MODEL slx_5f61af2557be
CONFIG AbsTol = auto
CONFIG EnableMultiTasking = off
CONFIG FixedStep = auto
CONFIG MaxStep = auto
CONFIG MinStep = auto
CONFIG RelTol = 1e-3
CONFIG SampleTimeConstraint = Unconstrained
CONFIG SolverName = ode23s
CONFIG StartTime = 0.0
CONFIG StopTime = 173.890
BLOCK [Constant] Constant
  Value = 0
BLOCK [Constant] Constant1
  Value = 0.013
BLOCK [FromWorkspace] From Workspace
  SampleTime = -1
  VariableName = pdl_percent
BLOCK [FromWorkspace] From Workspace1
  SampleTime = -1
  VariableName = left_mtr_tmp
BLOCK [FromWorkspace] From Workspace2
  VariableName = right_mtr_tmp
BLOCK [Gain] Gain
  Gain = 1/M
BLOCK [Gain] Gain2
  Gain = M/4*g
  NameLocation = right
BLOCK [Gain] Gain3
  Gain = 8.5/(M/4)
BLOCK [SubSystem] MATLAB Function2
  ErrorFcn = Stateflow.Translate.translate
  PermitHierarchicalResolution = ExplicitOnly
  SFBlockType = MATLAB Function
  TreatAsAtomicUnit = on
BLOCK [Demux] MATLAB Function2/ Demux 
  Outputs = 1
BLOCK [S-Function] MATLAB Function2/ SFunction 
  EnableBusSupport = on
  FunctionName = sf_sfun
  PortCounts = [2 2]
  SFcnIsStateOwnerBlock = off
  SFunctionDeploymentMode = off
  Tag = Stateflow S-Function 13
BLOCK [Terminator] MATLAB Function2/ Terminator 
BLOCK [Outport] MATLAB Function2/frr
BLOCK [Inport] MATLAB Function2/prev_wheel_ang_vel
BLOCK [Inport] MATLAB Function2/rolling_coeff
  Port = 2
BLOCK [Memory] Memory
BLOCK [SubSystem] Old_Slip_Controller
  PortSchema = {"entries":[{"content":{"sides":[{"content":{"connectorIds":["Out1"]},"type":"ConnectorPlacement.EquallySpacedRectSide","uuid":"3d629ccf-3120-465c-b95a-c1e856ea96ae"},{"content":{"side":"RIGHT"},"type":"ConnectorPlacement.EquallySpacedRectSide","uuid":"39ac0bf8-cdbe-4e91-b33c-4b222cbdbfda"},{"content":{"connectorIds":["In1","In2","In3"],"side":"TOP"},"type":"ConnectorPlacement.EquallySpacedRectSid...<+360ch>
BLOCK [Outport] Old_Slip_Controller/Error Torque
BLOCK [From] Old_Slip_Controller/From1
  GotoTag = slip_err
BLOCK [From] Old_Slip_Controller/From4
  GotoTag = curr_slip
BLOCK [Gain] Old_Slip_Controller/Gain
  Gain = 1/10
BLOCK [Gain] Old_Slip_Controller/Gain2
  Gain = 1/R
BLOCK [Goto] Old_Slip_Controller/Goto
  GotoTag = pid_slip_err
BLOCK [Goto] Old_Slip_Controller/Goto1
  GotoTag = slip_err
BLOCK [Goto] Old_Slip_Controller/Goto3
  GotoTag = curr_slip
BLOCK [Reference] Old_Slip_Controller/PID Controller (2DOF)  REF=slpidlib/PID Controller (2DOF)
  LibrarySourceBlock = simulink/Continuous/PID Controller (2DOF)
  SourceBlock = slpidlib/PID Controller (2DOF)
  SourceType = PID 2dof
BLOCK [Sum] Old_Slip_Controller/Subtract1
  IconShape = rectangular
  Inputs = +-
BLOCK [SubSystem] Old_Slip_Controller/Vehicle_vel_x_err
  ErrorFcn = Stateflow.Translate.translate
  PermitHierarchicalResolution = ExplicitOnly
  SFBlockType = MATLAB Function
  TreatAsAtomicUnit = on
BLOCK [Demux] Old_Slip_Controller/Vehicle_vel_x_err/ Demux 
  Outputs = 1
BLOCK [S-Function] Old_Slip_Controller/Vehicle_vel_x_err/ SFunction 
  EnableBusSupport = on
  FunctionName = sf_sfun
  PortCounts = [3 2]
  SFcnIsStateOwnerBlock = off
  SFunctionDeploymentMode = off
  Tag = Stateflow S-Function 4
BLOCK [Terminator] Old_Slip_Controller/Vehicle_vel_x_err/ Terminator 
BLOCK [Inport] Old_Slip_Controller/Vehicle_vel_x_err/accel_x
  Port = 3
BLOCK [Outport] Old_Slip_Controller/Vehicle_vel_x_err/err_veh_speed_x
BLOCK [Inport] Old_Slip_Controller/Vehicle_vel_x_err/pid_slip_err
BLOCK [Inport] Old_Slip_Controller/Vehicle_vel_x_err/wheel_speed_x
  Port = 2
BLOCK [Inport] Old_Slip_Controller/curr_slip_ratio
  Port = 3
BLOCK [Constant] Old_Slip_Controller/ideal_slip
  Value = 0.05
BLOCK [Scope] Old_Slip_Controller/slip_err
  Floating = off
  NumInputPorts = 4
  ScopeSpecificationString = Simulink.scopes.TimeScopeBlockCfg('CurrentConfiguration', extmgr.ConfigurationSet(extmgr.Configuration('Core','General UI',true),extmgr.Configuration('Core','Source UI',true),extmgr.Configuration('Sources','WiredSimulink',true,'DataLoggingVariableName','ScopeData1'),extmgr.Configuration('Visuals','Time Domain',true,'SerializedDisplays',{struct('MinYLimReal','-0.14568','MaxYLimReal','0.05647','YLab...<+1578ch>
BLOCK [Scope] Old_Slip_Controller/speed//accel-comparison
  Floating = off
  NumInputPorts = 4
  ScopeSpecificationString = Simulink.scopes.TimeScopeBlockCfg('CurrentConfiguration', extmgr.ConfigurationSet(extmgr.Configuration('Core','General UI',true),extmgr.Configuration('Core','Source UI',true),extmgr.Configuration('Sources','WiredSimulink',true,'DataLoggingVariableName','ScopeData2'),extmgr.Configuration('Visuals','Time Domain',true,'SerializedDisplays',{struct('MinYLimReal','62.2804','MaxYLimReal','173.12651','YLa...<+1560ch>
BLOCK [Constant] Old_Slip_Controller/target_err
  Value = 0
BLOCK [Inport] Old_Slip_Controller/vehicle_accel_x
BLOCK [Inport] Old_Slip_Controller/wheel_v_x
  Port = 2
BLOCK [Saturate] Saturation
  LowerLimit = 0
  UpperLimit = 1
BLOCK [Scope] Scope
  Floating = off
  NumInputPorts = 3
  ScopeSpecificationString = Simulink.scopes.TimeScopeBlockCfg('CurrentConfiguration', extmgr.ConfigurationSet(extmgr.Configuration('Core','General UI',true),extmgr.Configuration('Core','Source UI',true),extmgr.Configuration('Sources','WiredSimulink',true,'DataLoggingVariableName','ScopeData1'),extmgr.Configuration('Visuals','Time Domain',true,'SerializedDisplays',{struct('MinYLimReal','-1.9125','MaxYLimReal','17.2125','YLabe...<+1499ch>
BLOCK [Scope] Scope1
  Floating = off
  NumInputPorts = 1
  ScopeSpecificationString = Simulink.scopes.TimeScopeBlockCfg('CurrentConfiguration', extmgr.ConfigurationSet(extmgr.Configuration('Core','General UI',true),extmgr.Configuration('Core','Source UI',true),extmgr.Configuration('Sources','WiredSimulink',true,'DataLoggingVariableName','ScopeData1'),extmgr.Configuration('Visuals','Time Domain',true,'SerializedDisplays',{struct('MinYLimReal','-0.04536','MaxYLimReal','0.40826','YLab...<+1463ch>
BLOCK [SubSystem] Slip Controller 
  PortSchema = {"entries":[{"content":{"sides":[{"content":{"connectorIds":["Out1"]},"type":"ConnectorPlacement.EquallySpacedRectSide","uuid":"9ab017ca-b6c6-4a97-8642-adcc6752da5c"},{"content":{"connectorIds":["In1"],"side":"RIGHT"},"type":"ConnectorPlacement.EquallySpacedRectSide","uuid":"f028d533-9454-44bd-bcae-05da9a7b9b8f"},{"content":{"side":"TOP"},"type":"ConnectorPlacement.EquallySpacedRectSide","uuid":"7...<+348ch>
BLOCK [From] Slip Controller /From
  GotoTag = ideal_slip_ratio
BLOCK [Goto] Slip Controller /Goto
  GotoTag = ideal_slip_ratio
BLOCK [Reference] Slip Controller /PID Controller (2DOF)  REF=slpidlib/PID Controller (2DOF)
  LibrarySourceBlock = simulink/Continuous/PID Controller (2DOF)
  SourceBlock = slpidlib/PID Controller (2DOF)
  SourceType = PID 2dof
BLOCK [Sum] Slip Controller /Sum
  Inputs = |+-
BLOCK [Outport] Slip Controller /T_correction
BLOCK [Inport] Slip Controller /curr_slip
BLOCK [Constant] Slip Controller /ideal slip
  Value = 0.05
BLOCK [Scope] Slip Controller /slip
  Floating = off
  NumInputPorts = 3
  ScopeSpecificationString = Simulink.scopes.TimeScopeBlockCfg('CurrentConfiguration', extmgr.ConfigurationSet(extmgr.Configuration('Core','General UI',true),extmgr.Configuration('Core','Source UI',true),extmgr.Configuration('Sources','WiredSimulink',true,'DataLoggingVariableName','ScopeData1'),extmgr.Configuration('Visuals','Time Domain',true,'SerializedDisplays',{struct('MinYLimReal','-0.08166','MaxYLimReal','0.08642','YLab...<+1556ch>
BLOCK [Sum] Sum
  Inputs = |+-
BLOCK [Sum] Sum1
  Inputs = |-+
BLOCK [Sum] T_err
  Inputs = |+-
BLOCK [SubSystem] Torque Controller
BLOCK [Constant] Torque Controller/Car_Power_Limit_kW
  Value = 40
BLOCK [Constant] Torque Controller/Constant
BLOCK [Constant] Torque Controller/Constant1
  Value = 80.0/30.0
BLOCK [SubSystem] Torque Controller/MATLAB Function
  ErrorFcn = Stateflow.Translate.translate
  PermitHierarchicalResolution = ExplicitOnly
  SFBlockType = MATLAB Function
  TreatAsAtomicUnit = on
BLOCK [Demux] Torque Controller/MATLAB Function/ Demux 
  Outputs = 1
BLOCK [S-Function] Torque Controller/MATLAB Function/ SFunction 
  EnableBusSupport = on
  FunctionName = sf_sfun
  PortCounts = [3 2]
  SFcnIsStateOwnerBlock = off
  SFunctionDeploymentMode = off
  Tag = Stateflow S-Function 9
BLOCK [Terminator] Torque Controller/MATLAB Function/ Terminator 
BLOCK [Inport] Torque Controller/MATLAB Function/conversion_factor
  Port = 2
BLOCK [Inport] Torque Controller/MATLAB Function/inverter_power
BLOCK [Outport] Torque Controller/MATLAB Function/motor_RPM
BLOCK [Inport] Torque Controller/MATLAB Function/torque_request
  Port = 3
BLOCK [MinMax] Torque Controller/Max
  Function = max
  Inputs = 2
BLOCK [MinMax] Torque Controller/Max_Allowable_Power
  Inputs = 2
BLOCK [MinMax] Torque Controller/Max_Full_Throttle_Power
  Inputs = 2
BLOCK [SubSystem] Torque Controller/Max_Motor_Temp_Power
  ErrorFcn = Stateflow.Translate.translate
  PermitHierarchicalResolution = ExplicitOnly
  SFBlockType = MATLAB Function
  TreatAsAtomicUnit = on
BLOCK [Demux] Torque Controller/Max_Motor_Temp_Power/ Demux 
  Outputs = 1
BLOCK [S-Function] Torque Controller/Max_Motor_Temp_Power/ SFunction 
  EnableBusSupport = on
  FunctionName = sf_sfun
  PortCounts = [4 2]
  SFcnIsStateOwnerBlock = off
  SFunctionDeploymentMode = off
  Tag = Stateflow S-Function 3
BLOCK [Terminator] Torque Controller/Max_Motor_Temp_Power/ Terminator 
BLOCK [Outport] Torque Controller/Max_Motor_Temp_Power/avail_power
BLOCK [Inport] Torque Controller/Max_Motor_Temp_Power/curr_power_limit
  Port = 4
BLOCK [Inport] Torque Controller/Max_Motor_Temp_Power/decrementing_ratio
BLOCK [Inport] Torque Controller/Max_Motor_Temp_Power/max_motor_temp
  Port = 2
BLOCK [Inport] Torque Controller/Max_Motor_Temp_Power/motor_cutoff_temp
  Port = 3
BLOCK [Product] Torque Controller/Pedal_Based_Power_Request
BLOCK [SubSystem] Torque Controller/Pedal_Based_Torque_Mapping
  ErrorFcn = Stateflow.Translate.translate
  PermitHierarchicalResolution = ExplicitOnly
  SFBlockType = MATLAB Function
  TreatAsAtomicUnit = on
BLOCK [Demux] Torque Controller/Pedal_Based_Torque_Mapping/ Demux 
  Outputs = 1
BLOCK [S-Function] Torque Controller/Pedal_Based_Torque_Mapping/ SFunction 
  EnableBusSupport = on
  FunctionName = sf_sfun
  PortCounts = [1 2]
  SFcnIsStateOwnerBlock = off
  SFunctionDeploymentMode = off
  Tag = Stateflow S-Function 8
BLOCK [Terminator] Torque Controller/Pedal_Based_Torque_Mapping/ Terminator 
BLOCK [Outport] Torque Controller/Pedal_Based_Torque_Mapping/T
BLOCK [Inport] Torque Controller/Pedal_Based_Torque_Mapping/p_a
BLOCK [SubSystem] Torque Controller/Power_To_Torque
  ErrorFcn = Stateflow.Translate.translate
  PermitHierarchicalResolution = ExplicitOnly
  SFBlockType = MATLAB Function
  TreatAsAtomicUnit = on
BLOCK [Demux] Torque Controller/Power_To_Torque/ Demux 
  Outputs = 1
BLOCK [S-Function] Torque Controller/Power_To_Torque/ SFunction 
  EnableBusSupport = on
  FunctionName = sf_sfun
  PortCounts = [6 2]
  SFcnIsStateOwnerBlock = off
  SFunctionDeploymentMode = off
  Tag = Stateflow S-Function 7
BLOCK [Terminator] Torque Controller/Power_To_Torque/ Terminator 
BLOCK [Outport] Torque Controller/Power_To_Torque/Power_to_Torque
BLOCK [Inport] Torque Controller/Power_To_Torque/cl
  Port = 4
BLOCK [Inport] Torque Controller/Power_To_Torque/cr
  Port = 5
BLOCK [Inport] Torque Controller/Power_To_Torque/left_motor_speed
BLOCK [Inport] Torque Controller/Power_To_Torque/p_to_t_conversion_factor
  Port = 6
BLOCK [Inport] Torque Controller/Power_To_Torque/power_KW_input
  Port = 3
BLOCK [Inport] Torque Controller/Power_To_Torque/right_motor_speed
  Port = 2
BLOCK [Scope] Torque Controller/Scope
  Floating = off
  NumInputPorts = 3
  ScopeSpecificationString = Simulink.scopes.TimeScopeBlockCfg('CurrentConfiguration', extmgr.ConfigurationSet(extmgr.Configuration('Core','General UI',true),extmgr.Configuration('Core','Source UI',true),extmgr.Configuration('Sources','WiredSimulink',true,'DataLoggingVariableName','ScopeData1'),extmgr.Configuration('Visuals','Time Domain',true,'SerializedDisplays',{struct('MinYLimReal','-11.25','MaxYLimReal','101.25','YLabelR...<+1624ch>
BLOCK [SubSystem] Torque Controller/Steering_Angle_To_Delta
  ErrorFcn = Stateflow.Translate.translate
  PermitHierarchicalResolution = ExplicitOnly
  SFBlockType = MATLAB Function
  TreatAsAtomicUnit = on
BLOCK [Demux] Torque Controller/Steering_Angle_To_Delta/ Demux 
  Outputs = 1
BLOCK [S-Function] Torque Controller/Steering_Angle_To_Delta/ SFunction 
  EnableBusSupport = on
  FunctionName = sf_sfun
  PortCounts = [3 2]
  SFcnIsStateOwnerBlock = off
  SFunctionDeploymentMode = off
  Tag = Stateflow S-Function 6
BLOCK [Terminator] Torque Controller/Steering_Angle_To_Delta/ Terminator 
BLOCK [Inport] Torque Controller/Steering_Angle_To_Delta/TRACK_WIDTH_mm
  Port = 2
BLOCK [Inport] Torque Controller/Steering_Angle_To_Delta/WHEELBASE_mm
  Port = 3
BLOCK [Outport] Torque Controller/Steering_Angle_To_Delta/delta
BLOCK [Inport] Torque Controller/Steering_Angle_To_Delta/wheel_angle_deg
BLOCK [Sum] Torque Controller/Sum
  Inputs = |++
BLOCK [Sum] Torque Controller/Sum1
  Inputs = |+-
BLOCK [SubSystem] Torque Controller/Torque_To_Send
  ErrorFcn = Stateflow.Translate.translate
  PermitHierarchicalResolution = ExplicitOnly
  SFBlockType = MATLAB Function
  TreatAsAtomicUnit = on
BLOCK [Demux] Torque Controller/Torque_To_Send/ Demux 
  Outputs = 1
BLOCK [S-Function] Torque Controller/Torque_To_Send/ SFunction 
  EnableBusSupport = on
  FunctionName = sf_sfun
  PortCounts = [4 2]
  SFcnIsStateOwnerBlock = off
  SFunctionDeploymentMode = off
  Tag = Stateflow S-Function 5
BLOCK [Terminator] Torque Controller/Torque_To_Send/ Terminator 
BLOCK [Inport] Torque Controller/Torque_To_Send/cl
BLOCK [Outport] Torque Controller/Torque_To_Send/computed_torque
BLOCK [Inport] Torque Controller/Torque_To_Send/cr
  Port = 2
BLOCK [Inport] Torque Controller/Torque_To_Send/request_torque
  Port = 3
BLOCK [Inport] Torque Controller/Torque_To_Send/torque_lim
  Port = 4
BLOCK [Constant] Torque Controller/Track_width_mm
  Value = 1100
BLOCK [Constant] Torque Controller/Track_width_mm1
  Value = 1550
BLOCK [Outport] Torque Controller/computedTorque
BLOCK [Inport] Torque Controller/input
BLOCK [Inport] Torque Controller/left_motor_temp
  Port = 3
BLOCK [Inport] Torque Controller/motor_cutoff_temp
  Port = 2
BLOCK [Constant] Torque Controller/p2t_conversion_factor
  Value = 9550
BLOCK [Inport] Torque Controller/right_motor_temp
  Port = 4
BLOCK [Inport] Torque Controller/wheel_angle_deg
  Port = 5
BLOCK [Inport] Torque Controller/wheel_v_x
  Port = 6
BLOCK [MinMax] clamp1
  Function = max
  Inputs = 2
BLOCK [MinMax] clamp2
  Inputs = 2
BLOCK [Constant] cutoff_temp
  Value = 90
BLOCK [Gain] drag_f_form
  Gain = 0.5* mass_den * Cd * Af
BLOCK [Constant] max_torque
  Value = 90
BLOCK [Constant] min_torque
  Value = 0
BLOCK [Math] square
  Operator = square
BLOCK [SubSystem] tire_model
BLOCK [Constant] tire_model/Constant
  Value = 0
BLOCK [Outport] tire_model/F_x
  Port = 2
BLOCK [From] tire_model/From
  GotoTag = vehicle_v_x
  NameLocation = top
BLOCK [From] tire_model/From F_x
  GotoTag = F_x
BLOCK [FromWorkspace] tire_model/From Workspace
  SampleTime = -1
  VariableName = recorded_vel
BLOCK [From] tire_model/From1
  GotoTag = vehicle_a_x
  NameLocation = top
BLOCK [From] tire_model/From2
  GotoTag = slip_ratio
BLOCK [From] tire_model/From3
  GotoTag = wheel_ang_v_x
BLOCK [From] tire_model/From4
  GotoTag = vehicle_v_x
BLOCK [Gain] tire_model/Gain
  Gain = 1/J_w
BLOCK [Gain] tire_model/Gain1
  Gain = R
BLOCK [Gain] tire_model/Gain2
  Gain = M/4*g
  NameLocation = top
BLOCK [Gain] tire_model/Gain4
  Gain = R
  NameLocation = right
BLOCK [Goto] tire_model/Goto
  GotoTag = vehicle_a_x
BLOCK [Goto] tire_model/Goto1
  GotoTag = vehicle_v_x
BLOCK [Goto] tire_model/Goto2
  GotoTag = slip_ratio
BLOCK [Goto] tire_model/Goto3
  GotoTag = wheel_ang_v_x
BLOCK [Integrator] tire_model/Integrator
BLOCK [Integrator] tire_model/Integrator1
BLOCK [MinMax] tire_model/Max
  Function = max
  Inputs = 2
BLOCK [SubSystem] tire_model/Pacejka Magic Formula
  ErrorFcn = Stateflow.Translate.translate
  NameLocation = top
  PermitHierarchicalResolution = ExplicitOnly
  SFBlockType = MATLAB Function
  TreatAsAtomicUnit = on
BLOCK [Demux] tire_model/Pacejka Magic Formula/ Demux 
  Outputs = 1
BLOCK [S-Function] tire_model/Pacejka Magic Formula/ SFunction 
  EnableBusSupport = on
  FunctionName = sf_sfun
  Parameters = B,C,D,E
  PortCounts = [1 2]
  SFcnIsStateOwnerBlock = off
  SFunctionDeploymentMode = off
  Tag = Stateflow S-Function 1
BLOCK [Terminator] tire_model/Pacejka Magic Formula/ Terminator 
BLOCK [Outport] tire_model/Pacejka Magic Formula/friction_coeff
BLOCK [Inport] tire_model/Pacejka Magic Formula/lambda
BLOCK [Scope] tire_model/Scope
  Floating = off
  NumInputPorts = 2
  ScopeSpecificationString = Simulink.scopes.TimeScopeBlockCfg('CurrentConfiguration', extmgr.ConfigurationSet(extmgr.Configuration('Core','General UI',true),extmgr.Configuration('Core','Source UI',true),extmgr.Configuration('Sources','WiredSimulink',true,'DataLoggingVariableName','ScopeData1'),extmgr.Configuration('Visuals','Time Domain',true,'SerializedDisplays',{struct('MinYLimReal','-5.07777','MaxYLimReal','45.69989','YLa...<+1469ch>
BLOCK [Scope] tire_model/Slip & friction
  Floating = on
  NumInputPorts = 1
  ScopeSpecificationString = Simulink.scopes.TimeScopeBlockCfg('CurrentConfiguration', extmgr.ConfigurationSet(extmgr.Configuration('Core','General UI',true),extmgr.Configuration('Core','Source UI',true),extmgr.Configuration('Sources','WiredSimulink',true,'DataLoggingVariableName','ScopeData1'),extmgr.Configuration('Visuals','Time Domain',true,'SerializedDisplays',{struct('MinYLimReal','-0.08597','MaxYLimReal','0.7737','YLabe...<+1562ch>
BLOCK [Sum] tire_model/Sum
  Inputs = |+-
BLOCK [Inport] tire_model/T_in
  Port = 2
BLOCK [Scope] tire_model/Torques and speeds
  Floating = on
  NumInputPorts = 1
  ScopeSpecificationString = Simulink.scopes.TimeScopeBlockCfg('CurrentConfiguration', extmgr.ConfigurationSet(extmgr.Configuration('Core','General UI',true,'FigureColor',[0.156862745098039 0.156862745098039 0.156862745098039]),extmgr.Configuration('Core','Source UI',true),extmgr.Configuration('Sources','WiredSimulink',true,'DataLoggingSaveFormat','StructureWithTime','DataLoggingLimitDataPoints',true,'DataLoggingDecimation','...<+2887ch>
BLOCK [Goto] tire_model/goto F_x
  GotoTag = F_x
BLOCK [Outport] tire_model/slip_ratio
  Port = 4
BLOCK [SubSystem] tire_model/slip_ratio_calculation
  ErrorFcn = Stateflow.Translate.translate
  PermitHierarchicalResolution = ExplicitOnly
  SFBlockType = MATLAB Function
  TreatAsAtomicUnit = on
BLOCK [Demux] tire_model/slip_ratio_calculation/ Demux 
  Outputs = 1
BLOCK [S-Function] tire_model/slip_ratio_calculation/ SFunction 
  EnableBusSupport = on
  FunctionName = sf_sfun
  Parameters = TOL
  PortCounts = [3 2]
  SFcnIsStateOwnerBlock = off
  SFunctionDeploymentMode = off
  Tag = Stateflow S-Function 2
BLOCK [Terminator] tire_model/slip_ratio_calculation/ Terminator 
BLOCK [Outport] tire_model/slip_ratio_calculation/slip_ratio
BLOCK [Inport] tire_model/slip_ratio_calculation/vehicle_a_x
  Port = 3
BLOCK [Inport] tire_model/slip_ratio_calculation/vehicle_v_x
  Port = 2
BLOCK [Inport] tire_model/slip_ratio_calculation/wheel_v_x
BLOCK [Inport] tire_model/vehicle_a_x
BLOCK [Outport] tire_model/vehicle_v_x
BLOCK [Outport] tire_model/wheel_ang_v_x
  Port = 3
BLOCK [Outport] tire_model/wheel_v_x
  Port = 5
LINE Constant1:1 -> MATLAB Function2:2
LINE Constant:1 -> Torque Controller:5
LINE From Workspace1:1 -> Torque Controller:3
LINE From Workspace2:1 -> Torque Controller:4
LINE From Workspace:1 -> Saturation:1
LINE Gain2:1 -> Sum:2
LINE Gain3:1 -> Sum1:2
LINE Gain:1 -> Sum1:1
LINE MATLAB Function2:1 -> Gain2:1
LINE Memory:1 -> MATLAB Function2:1
LINE Old_Slip_Controller/From1:1 -> Old_Slip_Controller/slip_err:2
LINE Old_Slip_Controller/Gain2:1 -> Old_Slip_Controller/Gain:1
LINE Old_Slip_Controller/Gain:1 -> Old_Slip_Controller/Error Torque:1
LINE Old_Slip_Controller/Gain:1 -> Old_Slip_Controller/speed//accel-comparison:3
LINE Old_Slip_Controller/PID Controller (2DOF):1 -> Old_Slip_Controller/Goto:1
LINE Old_Slip_Controller/PID Controller (2DOF):1 -> Old_Slip_Controller/Vehicle_vel_x_err:1
LINE Old_Slip_Controller/Subtract1:1 -> Old_Slip_Controller/Goto1:1
LINE Old_Slip_Controller/Vehicle_vel_x_err:1 -> Old_Slip_Controller/Gain2:1
LINE Old_Slip_Controller/Vehicle_vel_x_err:1 -> Old_Slip_Controller/speed//accel-comparison:2
LINE Old_Slip_Controller/curr_slip_ratio:1 -> Old_Slip_Controller/Goto3:1
LINE Old_Slip_Controller/curr_slip_ratio:1 -> Old_Slip_Controller/PID Controller (2DOF):2
LINE Old_Slip_Controller/curr_slip_ratio:1 -> Old_Slip_Controller/Subtract1:2
LINE Old_Slip_Controller/ideal_slip:1 -> Old_Slip_Controller/PID Controller (2DOF):1
LINE Old_Slip_Controller/ideal_slip:1 -> Old_Slip_Controller/Subtract1:1
LINE Old_Slip_Controller/target_err:1 -> Old_Slip_Controller/slip_err:3
LINE Old_Slip_Controller/vehicle_accel_x:1 -> Old_Slip_Controller/Vehicle_vel_x_err:3
LINE Old_Slip_Controller/wheel_v_x:1 -> Old_Slip_Controller/Vehicle_vel_x_err:2
LINE Old_Slip_Controller/wheel_v_x:1 -> Old_Slip_Controller/speed//accel-comparison:1
LINE Saturation:1 -> Scope1:1
LINE Saturation:1 -> Torque Controller:1
LINE Slip Controller /From:1 -> Slip Controller /PID Controller (2DOF):1
LINE Slip Controller /PID Controller (2DOF):1 -> Slip Controller /T_correction:1
LINE Slip Controller /Sum:1 -> Slip Controller /slip:2
LINE Slip Controller /curr_slip:1 -> Slip Controller /PID Controller (2DOF):2
LINE Slip Controller /curr_slip:1 -> Slip Controller /Sum:2
LINE Slip Controller /curr_slip:1 -> Slip Controller /slip:3
LINE Slip Controller /ideal slip:1 -> Slip Controller /Goto:1
LINE Slip Controller /ideal slip:1 -> Slip Controller /Sum:1
LINE Slip Controller /ideal slip:1 -> Slip Controller /slip:1
LINE Slip Controller :1 -> T_err:2
LINE Sum1:1 -> tire_model:1
LINE Sum:1 -> Gain3:1
LINE T_err:1 -> clamp1:2
LINE Torque Controller/Car_Power_Limit_kW:1 -> Torque Controller/Max_Full_Throttle_Power:2
LINE Torque Controller/Car_Power_Limit_kW:1 -> Torque Controller/Max_Motor_Temp_Power:4
LINE Torque Controller/Car_Power_Limit_kW:1 -> Torque Controller/Pedal_Based_Power_Request:1
LINE Torque Controller/Constant1:1 -> Torque Controller/Max_Motor_Temp_Power:1
LINE Torque Controller/Constant:1 -> Torque Controller/Sum1:1
LINE Torque Controller/Constant:1 -> Torque Controller/Sum:1
LINE Torque Controller/MATLAB Function:1 -> Torque Controller/Power_To_Torque:1
LINE Torque Controller/MATLAB Function:1 -> Torque Controller/Power_To_Torque:2
LINE Torque Controller/Max:1 -> Torque Controller/Max_Motor_Temp_Power:2
LINE Torque Controller/Max_Allowable_Power:1 -> Torque Controller/MATLAB Function:1
LINE Torque Controller/Max_Allowable_Power:1 -> Torque Controller/Power_To_Torque:3
LINE Torque Controller/Max_Full_Throttle_Power:1 -> Torque Controller/Max_Allowable_Power:1
LINE Torque Controller/Max_Motor_Temp_Power:1 -> Torque Controller/Max_Full_Throttle_Power:1
LINE Torque Controller/Pedal_Based_Power_Request:1 -> Torque Controller/Max_Allowable_Power:2
LINE Torque Controller/Pedal_Based_Torque_Mapping:1 -> Torque Controller/MATLAB Function:3
LINE Torque Controller/Pedal_Based_Torque_Mapping:1 -> Torque Controller/Scope:3
LINE Torque Controller/Pedal_Based_Torque_Mapping:1 -> Torque Controller/Torque_To_Send:3
LINE Torque Controller/Power_To_Torque:1 -> Torque Controller/Scope:2
LINE Torque Controller/Power_To_Torque:1 -> Torque Controller/Torque_To_Send:4
LINE Torque Controller/Steering_Angle_To_Delta:1 -> Torque Controller/Sum1:2
LINE Torque Controller/Steering_Angle_To_Delta:1 -> Torque Controller/Sum:2
LINE Torque Controller/Sum1:1 -> Torque Controller/Power_To_Torque:5
LINE Torque Controller/Sum1:1 -> Torque Controller/Torque_To_Send:2
LINE Torque Controller/Sum:1 -> Torque Controller/Power_To_Torque:4
LINE Torque Controller/Sum:1 -> Torque Controller/Torque_To_Send:1
LINE Torque Controller/Torque_To_Send:1 -> Torque Controller/Scope:1
LINE Torque Controller/Torque_To_Send:1 -> Torque Controller/computedTorque:1
LINE Torque Controller/Track_width_mm1:1 -> Torque Controller/Steering_Angle_To_Delta:3
LINE Torque Controller/Track_width_mm:1 -> Torque Controller/Steering_Angle_To_Delta:2
LINE Torque Controller/input:1 -> Torque Controller/Pedal_Based_Power_Request:2
LINE Torque Controller/input:1 -> Torque Controller/Pedal_Based_Torque_Mapping:1
LINE Torque Controller/left_motor_temp:1 -> Torque Controller/Max:1
LINE Torque Controller/motor_cutoff_temp:1 -> Torque Controller/Max_Motor_Temp_Power:3
LINE Torque Controller/p2t_conversion_factor:1 -> Torque Controller/MATLAB Function:2
LINE Torque Controller/p2t_conversion_factor:1 -> Torque Controller/Power_To_Torque:6
LINE Torque Controller/right_motor_temp:1 -> Torque Controller/Max:2
LINE Torque Controller/wheel_angle_deg:1 -> Torque Controller/Steering_Angle_To_Delta:1
LINE Torque Controller:1 -> Scope:1
LINE Torque Controller:1 -> T_err:1
LINE clamp1:1 -> clamp2:2
LINE clamp2:1 -> Scope:3
LINE clamp2:1 -> tire_model:2
LINE cutoff_temp:1 -> Torque Controller:2
LINE drag_f_form:1 -> Gain:1
LINE max_torque:1 -> clamp2:1
LINE min_torque:1 -> clamp1:1
LINE square:1 -> drag_f_form:1
LINE tire_model/Constant:1 -> tire_model/Max:1
LINE tire_model/From F_x:1 -> tire_model/F_x:1
LINE tire_model/From Workspace:1 -> tire_model/Max:2
LINE tire_model/From1:1 -> tire_model/slip_ratio_calculation:3
LINE tire_model/From2:1 -> tire_model/slip_ratio:1
LINE tire_model/From3:1 -> tire_model/wheel_ang_v_x:1
LINE tire_model/From4:1 -> tire_model/Scope:1
LINE tire_model/From:1 -> tire_model/slip_ratio_calculation:2
LINE tire_model/From:1 -> tire_model/vehicle_v_x:1
LINE tire_model/Gain1:1 -> tire_model/slip_ratio_calculation:1
LINE tire_model/Gain1:1 -> tire_model/wheel_v_x:1
LINE tire_model/Gain2:1 -> tire_model/Gain4:1
LINE tire_model/Gain2:1 -> tire_model/goto F_x:1
LINE tire_model/Gain4:1 -> tire_model/Sum:2
LINE tire_model/Gain:1 -> tire_model/Integrator:1
LINE tire_model/Integrator1:1 -> tire_model/Goto1:1
LINE tire_model/Integrator:1 -> tire_model/Gain1:1
LINE tire_model/Integrator:1 -> tire_model/Goto3:1
LINE tire_model/Max:1 -> tire_model/Scope:2
LINE tire_model/Pacejka Magic Formula:1 -> tire_model/Gain2:1
LINE tire_model/Sum:1 -> tire_model/Gain:1
LINE tire_model/T_in:1 -> tire_model/Sum:1
LINE tire_model/slip_ratio_calculation:1 -> tire_model/Goto2:1
LINE tire_model/slip_ratio_calculation:1 -> tire_model/Pacejka Magic Formula:1
LINE tire_model/vehicle_a_x:1 -> tire_model/Goto:1
LINE tire_model/vehicle_a_x:1 -> tire_model/Integrator1:1
LINE tire_model:1 -> square:1
LINE tire_model:2 -> Sum:1
LINE tire_model:3 -> Memory:1
LINE tire_model:4 -> Slip Controller :1
LINE tire_model:5 -> Torque Controller:6
CHART MATLAB Function2 states=1 transitions=1
  STATE_LABEL 'eML_blk_kernel()'
  STATE_LABEL "SCRIPT:\nfunction frr = fcn(prev_wheel_ang_vel, rolling_coeff)\n\n% no physics formula to refer for this however I did this based on\n% intuition... essentially I don't believe rolling resistance should be\n% effecting the friction force on the car if the wheels are not moving\n\nif(prev_wheel_ang_vel <= 0)\n    frr = 0;\nelse\n    frr = rolling_coeff; \nend\n"
CHART tire_model/Pacejka Magic Formula states=1 transitions=1
  STATE_LABEL 'eML_blk_kernel()'
  STATE_LABEL 'SCRIPT:\nfunction friction_coeff = fcn(lambda, B, C, D, E)\n\nfriction_coeff = D*sin(C*atan(B*lambda -  E*(B*lambda - atan(B*lambda))));'
CHART tire_model/slip_ratio_calculation states=1 transitions=1
  STATE_LABEL 'eML_blk_kernel()'
  STATE_LABEL 'SCRIPT:\nfunction slip_ratio = fcn(wheel_v_x, vehicle_v_x, TOL, vehicle_a_x)\n% This is derived from pg. 100 of Rajamani - Vehicle Dynamics and Control\n% (2006)\n\nif vehicle_a_x >= 0\n    slip_ratio = (wheel_v_x - vehicle_v_x)/(wheel_v_x + TOL);\nelse\n    slip_ratio = (wheel_v_x - vehicle_v_x)/(vehicle_v_x + TOL);\nend'
CHART Torque Controller/Max_Motor_Temp_Power states=1 transitions=1
  STATE_LABEL 'eML_blk_kernel()'
  STATE_LABEL 'SCRIPT:\nfunction avail_power = fcn( decrementing_ratio,max_motor_temp, ...\n    motor_cutoff_temp, curr_power_limit)\n\navail_power = curr_power_limit;\n\nif (max_motor_temp - motor_cutoff_temp) >= 30.0\n    avail_power = 0.0;\nelseif max_motor_temp > motor_cutoff_temp\n    avail_power = curr_power_limit - ...\n    (max_motor_temp - motor_cutoff_temp) * ...\n    decrementing_ratio;\nend\n\n'
CHART Old_Slip_Controller/Vehicle_vel_x_err states=1 transitions=1
  STATE_LABEL 'eML_blk_kernel()'
  STATE_LABEL "SCRIPT:\nfunction err_veh_speed_x = fcn(pid_slip_err, wheel_speed_x, accel_x)\n \n\n% formula used for calcualtion is slip = \n% (wheel_speed - vehicle_speed)/(vehicle or wheel speed depending on acel)\n% we'll use the same calculation calulcation to calculate an error vehicle\n% speed.. this will then need to be converted to an error torque\n\n% when postively accelrating the tires tries spin faster than ...<+436ch>"
CHART Torque Controller/Torque_To_Send states=1 transitions=1
  STATE_LABEL 'eML_blk_kernel()'
  STATE_LABEL 'SCRIPT:\n% this block should theoritically not do anything as of now because of the\n% way motor speed was calculate (the output of maxPower_to_Torque is going\n% to be requested torque as of now)\n\nfunction computed_torque = fcn(cl, cr, request_torque, torque_lim)\n\n% will be the same for now \ntorque_left_nm = request_torque * cl; \ntorque_right_nm = request_torque * cr; \nscale = 1.0; \n\ntorque_req_max ...<+163ch>'
CHART Torque Controller/Steering_Angle_To_Delta states=1 transitions=1
  STATE_LABEL 'eML_blk_kernel()'
  STATE_LABEL 'SCRIPT:\nfunction delta = fcn(wheel_angle_deg, TRACK_WIDTH_mm, WHEELBASE_mm)\n\ndelta = TRACK_WIDTH_mm * tan(deg2rad(wheel_angle_deg)) / (2 * WHEELBASE_mm);\n'
CHART Torque Controller/Power_To_Torque states=1 transitions=1
  STATE_LABEL 'eML_blk_kernel()'
  STATE_LABEL 'SCRIPT:\nfunction Power_to_Torque = fcn(left_motor_speed, right_motor_speed,power_KW_input, ...\n    cl,cr, p_to_t_conversion_factor)\n\n% taken directly from code .. standard motor torque charac eqn assumes\n% torque is equally distributed between left and right wheel\n\n% since our power limit torque is calcuated using requested torque if we\n% use the name power to torque formula that we use in code we...<+600ch>'
CHART Torque Controller/Pedal_Based_Torque_Mapping states=1 transitions=1
  STATE_LABEL 'eML_blk_kernel()'
  STATE_LABEL 'SCRIPT:\nfunction T = fcn(p_a)\n\nT = 90*p_a;\n'
CHART Torque Controller/MATLAB Function states=1 transitions=1
  STATE_LABEL 'eML_blk_kernel()'
  STATE_LABEL 'SCRIPT:\nfunction motor_RPM = fcn(inverter_power, conversion_factor, torque_request)\n\n% kinda sus calculation but we need a way to calculate motor speed from\n% torque... decided to use W = 9550 * P in KW /T N in rpm \n% problem is the power_to_torque function just calculates using the same\n% formula so essentially it will go back to the torque request \n\nmotor_RPM = (inverter_power * conversion_facto...<+33ch>'
CHART  states=0 transitions=0
CHART  states=0 transitions=0
CHART  states=0 transitions=0
CHART  states=0 transitions=0
CHART  states=0 transitions=0
CHART  states=0 transitions=0
CHART  states=0 transitions=0
CHART  states=0 transitions=0
CHART  states=0 transitions=0
CHART  states=0 transitions=0
